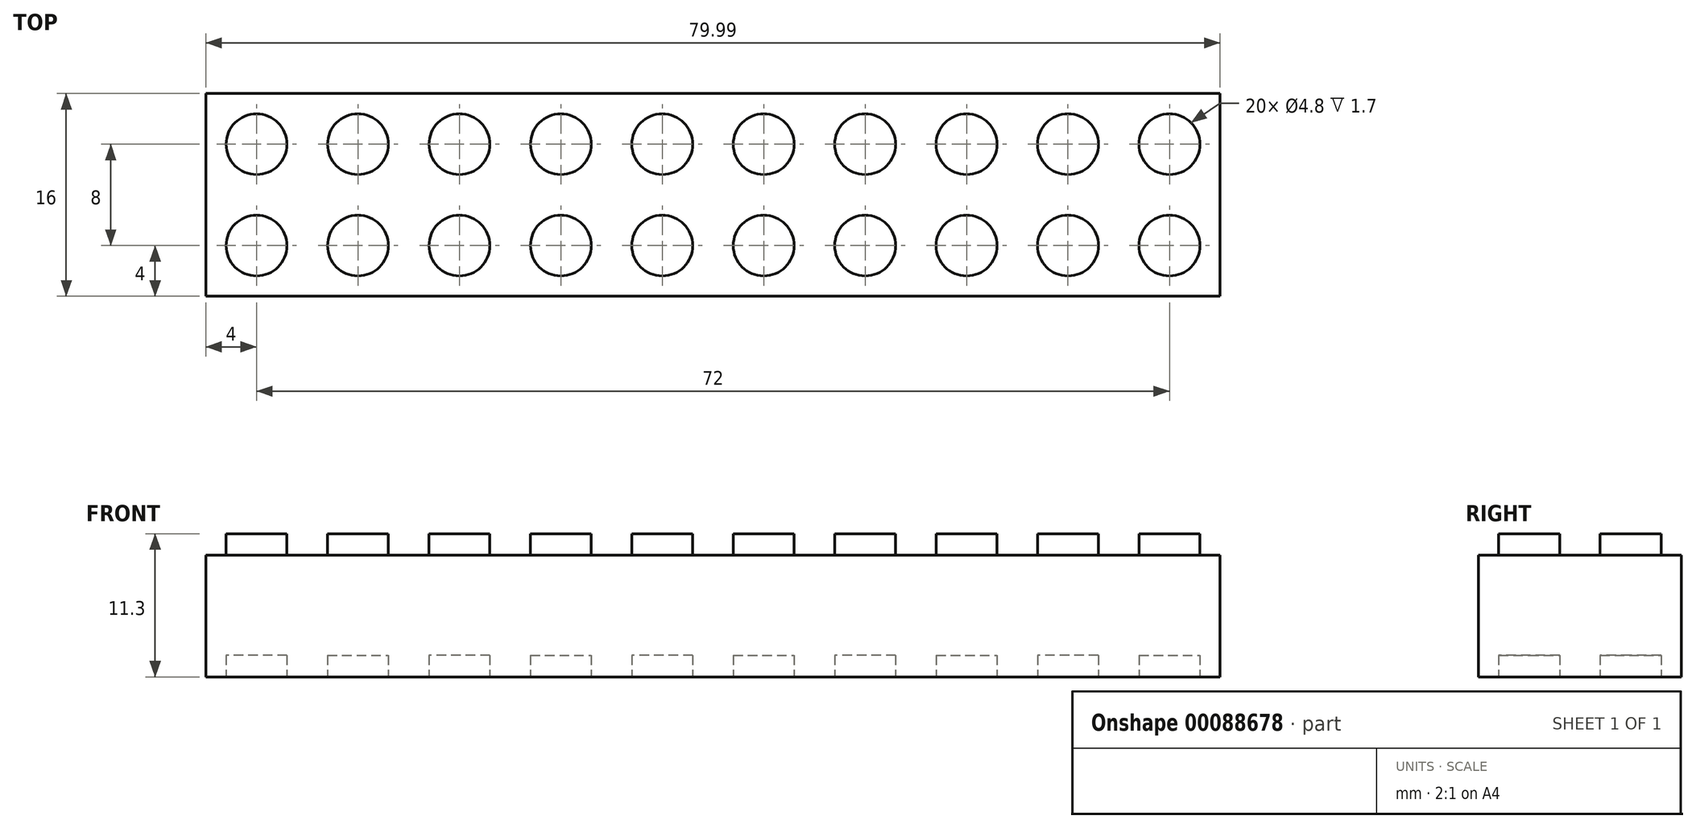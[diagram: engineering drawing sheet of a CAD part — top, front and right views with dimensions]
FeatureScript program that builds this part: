
annotation { "Feature Type Name" : "Feature", "Feature Type Description" : "" }
export const myFeature = defineFeature(function(context is Context, id is Id, definition is map)
    precondition{}
    {
        {
            var Q0;
            Q0=qCreatedBy(makeId("Front.planeOp"),FACE);
            var sketch = newSketch(context, id + "F0", { "sketchPlane" : qUnion([Q0])});
            skLineSegment(sketch, "E0.bottom", {"start": v(-4, 9.6) * mm, "end": v(-2.4, 9.6) * mm});
            skLineSegment(sketch, "E0.top", {"start": v(-4, 0) * mm, "end": v(4, 0) * mm});
            skLineSegment(sketch, "E0.left", {"start": v(-4, 9.6) * mm, "end": v(-4, 0) * mm});
            skLineSegment(sketch, "E0.right", {"start": v(4, 9.6) * mm, "end": v(4, 0) * mm});
            skLineSegment(sketch, "E1.top", {"start": v(-2.4, 11.3) * mm, "end": v(2.4, 11.3) * mm});
            skLineSegment(sketch, "E1.left", {"start": v(-2.4, 9.6) * mm, "end": v(-2.4, 11.3) * mm});
            skLineSegment(sketch, "E1.right", {"start": v(2.4, 9.6) * mm, "end": v(2.4, 11.3) * mm});
            skLineSegment(sketch, "E2", {"start": v(0, 0) * mm, "end": v(0, 24.04) * mm, "construction": true});
            skLineSegment(sketch, "E3.trimOffspring", {"start": v(2.4, 9.6) * mm, "end": v(4, 9.6) * mm});
            skSolve(sketch);
        }
        {
            var Q0;
            Q0=makeQuery(id+"F0.imprint","IMPRINT",FACE,{"disambiguationData":[TD([[makeQuery(id+"F0.imprint","IMPRINT",EDGE,{"derivedFrom":sQuery(id+"F0.wireOp",EDGE,"E0.bottom")}),-1.0]])]});
            extrude(context, id + "F1", {"entities" : qUnion([Q0]), "depth" : 8 * mm});
        }
        {
            var Q0;
            Q0=qCreatedBy(makeId("Top.planeOp"),FACE);
            var Q1;
            Q1=makeQuery(id+"F1.opExtrude","CAP_VERTEX",VERTEX,{"disambiguationData":[OSD([sQuery(id+"F0.wireOp",EDGE,"E1.top"),sQuery(id+"F0.wireOp",EDGE,"E1.right")])],"isStart":true});
            cPlane(context, id + "F2", {"entities" : qUnion([Q0, Q1]), "cplaneType" : CPlaneType.PLANE_POINT, "offset" : 152.4 * mm, "width" : 152.4 * mm, "height" : 152.4 * mm});
        }
        {
            var Q0;
            Q0=qCreatedBy(id+"F2.planeOp",FACE);
            var sketch = newSketch(context, id + "F3", { "sketchPlane" : qUnion([Q0])});
            skLineSegment(sketch, "E4.0", {"start": v(-4, -8) * mm, "end": v(-4, 0) * mm});
            skLineSegment(sketch, "E5.0", {"start": v(4, -8) * mm, "end": v(4, 0) * mm});
            skLineSegment(sketch, "E6", {"start": v(-4, 0) * mm, "end": v(4, 0) * mm});
            skLineSegment(sketch, "E7", {"start": v(-4, -8) * mm, "end": v(4, -8) * mm});
            skLineSegment(sketch, "E8", {"start": v(-4, 0) * mm, "end": v(4, -8) * mm, "construction": true});
            skLineSegment(sketch, "E9", {"start": v(-4, -8) * mm, "end": v(4, 0) * mm, "construction": true});
            skCircle(sketch, "E10", {"center": v(0, -4) * mm, "radius": 2.4 * mm});
            skSolve(sketch);
        }
        {
            var Q0;
            Q0=qSketchRegion(id+"F3",true);
            var Q1;
            Q1=makeQuery(id+"F1.opExtrude","SWEPT_FACE",FACE,{"disambiguationData":[OSD([sQuery(id+"F0.wireOp",EDGE,"E0.bottom")])]});
            extrude(context, id + "F4", {"entities" : qUnion([Q0]), "operationType" : NewBodyOperationType.REMOVE, "endBound" : BoundingType.UP_TO_SURFACE, "oppositeDirection" : true, "endBoundEntityFace" : qUnion([Q1]), "depth" : 25.4 * mm});
        }
        {
            var Q0;
            Q0=qCreatedBy(makeId("Top.planeOp"),FACE);
            var sketch = newSketch(context, id + "F5", { "sketchPlane" : qUnion([Q0])});
            skCircle(sketch, "E11.0", {"center": v(0, -4) * mm, "radius": 2.4 * mm});
            skSolve(sketch);
        }
        {
            var Q0;
            Q0=makeQuery(id+"F5.imprint","IMPRINT",FACE,{"disambiguationData":[TD([[makeQuery(id+"F5.imprint","IMPRINT",EDGE,{"derivedFrom":sQuery(id+"F5.wireOp",EDGE,"E11.0")}),1.0]])]});
            extrude(context, id + "F6", {"entities" : qUnion([Q0]), "operationType" : NewBodyOperationType.REMOVE, "depth" : 1.7 * mm});
        }
        {
            var Q0;
            Q0=qCreatedBy(makeId("Right.planeOp"),FACE);
            var Q1;
            Q1=makeQuery(id+"F1.opExtrude","CAP_VERTEX",VERTEX,{"disambiguationData":[OSD([sQuery(id+"F0.wireOp",EDGE,"E0.right"),sQuery(id+"F0.wireOp",EDGE,"E3.trimOffspring")])],"isStart":false});
            cPlane(context, id + "F7", {"entities" : qUnion([Q0, Q1]), "cplaneType" : CPlaneType.PLANE_POINT, "offset" : 152.4 * mm, "width" : 152.4 * mm, "height" : 152.4 * mm});
        }
        {
            var Q0;
            Q0=makeQuery(id+"F1.opExtrude","SWEPT_BODY",BODY,{"disambiguationData":[OSD([sQuery(id+"F0.wireOp",EDGE,"E0.bottom"),sQuery(id+"F0.wireOp",EDGE,"E0.top"),sQuery(id+"F0.wireOp",EDGE,"E0.left"),sQuery(id+"F0.wireOp",EDGE,"E0.right"),sQuery(id+"F0.wireOp",EDGE,"E1.top"),sQuery(id+"F0.wireOp",EDGE,"E1.left"),sQuery(id+"F0.wireOp",EDGE,"E1.right"),sQuery(id+"F0.wireOp",EDGE,"E3.trimOffspring")])]});
            var Q1;
            Q1=qCreatedBy(id+"F7.planeOp",FACE);
            mirror(context, id + "F8", {"operationType" : NewBodyOperationType.ADD, "entities" : qUnion([Q0]), "mirrorPlane" : qUnion([Q1])});
        }
        {
            var Q0;
            Q0=makeQuery(id+"F1.opExtrude","SWEPT_BODY",BODY,{"disambiguationData":[OSD([sQuery(id+"F0.wireOp",EDGE,"E0.bottom"),sQuery(id+"F0.wireOp",EDGE,"E0.top"),sQuery(id+"F0.wireOp",EDGE,"E0.left"),sQuery(id+"F0.wireOp",EDGE,"E0.right"),sQuery(id+"F0.wireOp",EDGE,"E1.top"),sQuery(id+"F0.wireOp",EDGE,"E1.left"),sQuery(id+"F0.wireOp",EDGE,"E1.right"),sQuery(id+"F0.wireOp",EDGE,"E3.trimOffspring")])]});
            var Q1;
            Q1=qCreatedBy(makeId("Front.planeOp"),FACE);
            mirror(context, id + "F9", {"operationType" : NewBodyOperationType.ADD, "entities" : qUnion([Q0]), "mirrorPlane" : qUnion([Q1])});
        }
        {
            var Q0;
            Q0=qCreatedBy(id+"F7.planeOp",FACE);
            var Q1;
            Q1=makeQuery(id+"F9.opPattern","COPY",VERTEX,{"derivedFrom":makeQuery(id+"F8.opPattern","COPY",VERTEX,{"derivedFrom":makeQuery(id+"F1.opExtrude","CAP_VERTEX",VERTEX,{"disambiguationData":[OSD([sQuery(id+"F0.wireOp",EDGE,"E0.bottom"),sQuery(id+"F0.wireOp",EDGE,"E0.left")])],"isStart":false}),"instanceName":"1"}),"instanceName":"1"});
            cPlane(context, id + "F10", {"entities" : qUnion([Q0, Q1]), "cplaneType" : CPlaneType.PLANE_POINT, "offset" : 152.4 * mm, "width" : 152.4 * mm, "height" : 152.4 * mm});
        }
        {
            var Q0;
            Q0=makeQuery(id+"F1.opExtrude","SWEPT_BODY",BODY,{"disambiguationData":[OSD([sQuery(id+"F0.wireOp",EDGE,"E0.bottom"),sQuery(id+"F0.wireOp",EDGE,"E0.top"),sQuery(id+"F0.wireOp",EDGE,"E0.left"),sQuery(id+"F0.wireOp",EDGE,"E0.right"),sQuery(id+"F0.wireOp",EDGE,"E1.top"),sQuery(id+"F0.wireOp",EDGE,"E1.left"),sQuery(id+"F0.wireOp",EDGE,"E1.right"),sQuery(id+"F0.wireOp",EDGE,"E3.trimOffspring")])]});
            var Q1;
            Q1=qCreatedBy(id+"F10.planeOp",FACE);
            mirror(context, id + "F11", {"operationType" : NewBodyOperationType.ADD, "entities" : qUnion([Q0]), "mirrorPlane" : qUnion([Q1])});
        }
        {
            var Q0;
            Q0=makeQuery(id+"F1.opExtrude","SWEPT_BODY",BODY,{"disambiguationData":[OSD([sQuery(id+"F0.wireOp",EDGE,"E0.bottom"),sQuery(id+"F0.wireOp",EDGE,"E0.top"),sQuery(id+"F0.wireOp",EDGE,"E0.left"),sQuery(id+"F0.wireOp",EDGE,"E0.right"),sQuery(id+"F0.wireOp",EDGE,"E1.top"),sQuery(id+"F0.wireOp",EDGE,"E1.left"),sQuery(id+"F0.wireOp",EDGE,"E1.right"),sQuery(id+"F0.wireOp",EDGE,"E3.trimOffspring")])]});
            var Q1;
            {var subQ0=makeQuery(id+"F1.opExtrude","SWEPT_FACE",FACE,{"disambiguationData":[OSD([sQuery(id+"F0.wireOp",EDGE,"E0.left")])]});Q1=makeQuery(id+"F11.opPattern","COPY",FACE,{"derivedFrom":makeQuery(id+"F9.boolean.opBoolean","MERGE",FACE,{"derivedFrom":[subQ0,makeQuery(id+"F9.opPattern","COPY",FACE,{"derivedFrom":subQ0,"instanceName":"1"})]}),"instanceName":"1"});}
            mirror(context, id + "F12", {"operationType" : NewBodyOperationType.ADD, "entities" : qUnion([Q0]), "mirrorPlane" : qUnion([Q1])});
        }
        {
            var Q0;
            Q0=makeQuery(id+"F1.opExtrude","SWEPT_BODY",BODY,{"disambiguationData":[OSD([sQuery(id+"F0.wireOp",EDGE,"E0.bottom"),sQuery(id+"F0.wireOp",EDGE,"E0.top"),sQuery(id+"F0.wireOp",EDGE,"E0.left"),sQuery(id+"F0.wireOp",EDGE,"E0.right"),sQuery(id+"F0.wireOp",EDGE,"E1.top"),sQuery(id+"F0.wireOp",EDGE,"E1.left"),sQuery(id+"F0.wireOp",EDGE,"E1.right"),sQuery(id+"F0.wireOp",EDGE,"E3.trimOffspring")])]});
            var Q1;
            {var subQ0=makeQuery(id+"F1.opExtrude","SWEPT_FACE",FACE,{"disambiguationData":[OSD([sQuery(id+"F0.wireOp",EDGE,"E0.left")])]});Q1=makeQuery(id+"F12.opPattern","COPY",FACE,{"derivedFrom":makeQuery(id+"F9.boolean.opBoolean","MERGE",FACE,{"derivedFrom":[subQ0,makeQuery(id+"F9.opPattern","COPY",FACE,{"derivedFrom":subQ0,"instanceName":"1"})]}),"instanceName":"1"});}
            mirror(context, id + "F13", {"operationType" : NewBodyOperationType.ADD, "entities" : qUnion([Q0]), "mirrorPlane" : qUnion([Q1])});
        }
        {
            var Q0;
            {var subQ0=makeQuery(id+"F1.opExtrude","SWEPT_FACE",FACE,{"disambiguationData":[OSD([sQuery(id+"F0.wireOp",EDGE,"E0.left")])]});Q0=makeQuery(id+"F13.opPattern","COPY",FACE,{"derivedFrom":makeQuery(id+"F9.boolean.opBoolean","MERGE",FACE,{"derivedFrom":[subQ0,makeQuery(id+"F9.opPattern","COPY",FACE,{"derivedFrom":subQ0,"instanceName":"1"})]}),"instanceName":"1"});}
            cPlane(context, id + "F14", {"entities" : qUnion([Q0]), "cplaneType" : CPlaneType.OFFSET, "offset" : 0 * mm, "width" : 152.4 * mm, "height" : 152.4 * mm});
        }
        {
            var Q0;
            Q0=qCreatedBy(id+"F14.planeOp",FACE);
            var sketch = newSketch(context, id + "F15", { "sketchPlane" : qUnion([Q0])});
            skLineSegment(sketch, "E12.bottom", {"start": v(15.13, 21.38) * mm, "end": v(-15.13, 21.38) * mm});
            skLineSegment(sketch, "E12.top", {"start": v(15.13, -12.18) * mm, "end": v(-15.13, -12.18) * mm});
            skLineSegment(sketch, "E12.left", {"start": v(15.13, 21.38) * mm, "end": v(15.13, -12.18) * mm});
            skLineSegment(sketch, "E12.right", {"start": v(-15.13, 21.38) * mm, "end": v(-15.13, -12.18) * mm});
            skPoint(sketch, "E12.middle", {"position": v(0, 4.6) * mm});
            skSolve(sketch);
        }
        {
            var Q0;
            Q0 = qSketchRegion(id + "F15", true);
            extrude(context, id + "F16", {"entities" : qUnion([Q0]), "operationType" : NewBodyOperationType.REMOVE, "oppositeDirection" : true, "depth" : 0.32 * 152.4 * mm, "offsetDistance" : 25.4 * mm});
        }
    });
